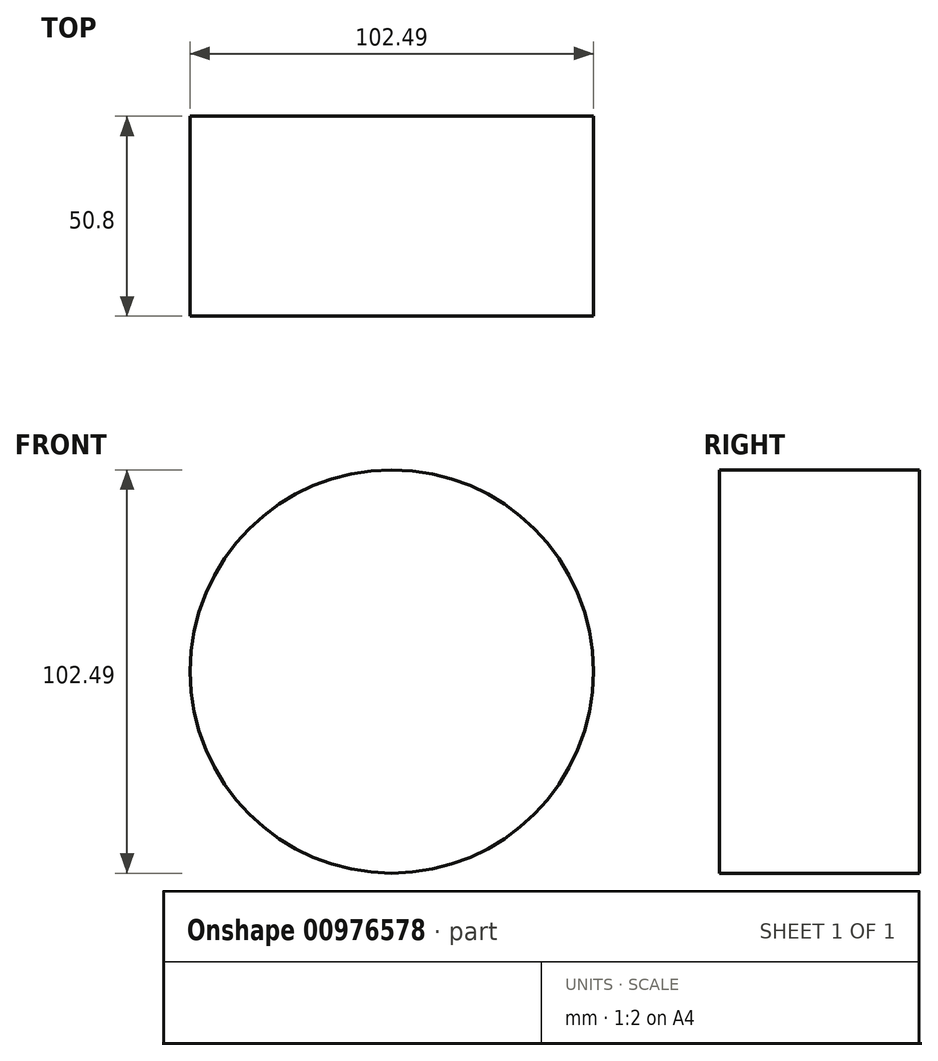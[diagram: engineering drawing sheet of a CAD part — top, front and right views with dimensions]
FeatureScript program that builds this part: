
annotation { "Feature Type Name" : "Feature", "Feature Type Description" : "" }
export const myFeature = defineFeature(function(context is Context, id is Id, definition is map)
    precondition{}
    {
        {
            var Q0;
            Q0=qCreatedBy(makeId("Front.planeOp"),FACE);
            var sketch = newSketch(context, id + "F0", { "sketchPlane" : qUnion([Q0])});
            skCircle(sketch, "E0", {"center": v(6.16, 5.23) * mm, "radius": 51.24 * mm});
            skSolve(sketch);
        }
        {
            var Q0;
            Q0 = qSketchRegion(id + "F0", true);
            extrude(context, id + "F1", {"entities" : qUnion([Q0]), "depth" : 50.8 * mm, "offsetDistance" : 25.4 * mm});
        }
    });
